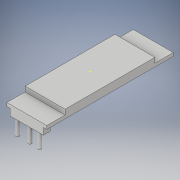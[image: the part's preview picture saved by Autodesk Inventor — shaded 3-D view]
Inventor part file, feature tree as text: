
AUTODESK INVENTOR PART (.ipt)
format: ipt  version: 2017.2 (Build 212223000, 223)  size: 128,000 bytes
history: native  units: in
note: dims shown in document units (in); Inventor stores cm internally (conversion verified against a paired STEP export)
features: sketch x7, extrude x4
ambient origin geometry x8: Origin, YZ Plane, XZ Plane, XY Plane, X Axis, Y Axis, Z Axis, Center Point
bodies: Solid1 (feature_tree)
feature tree (11):
  extrude  "Extrusion1"  Depth=0.4724in
  sketch  "Sketch2"  dims[d2=0.0394in d3=0.0in d4=1.063in]
  extrude  "Extrusion2"  Depth=1.063in
  sketch  "Sketch4"  dims[d11=0.1969in d12=0.0787in]
  sketch  "Sketch5"  dims[d13=0.1969in]
  extrude  "Extrusion3"  Depth=0.0591in TaperAngle=0.0deg
  extrude  "Extrusion4"  Depth=0.0787in
  sketch  "Sketch1"  dims[d0=1.4961in d1=0.4724in]
  sketch  "Sketch3"  dims[d5=0.4724in d6=0.0591in d7=0.0in]
  sketch  "Sketch6"  dims[d14=0.0787in d15=0.0in]
  sketch  "Sketch7"  dims[d16=0.0394in d17=0.0394in d18=0.0394in d19=0.1969in d20=0.0in]
